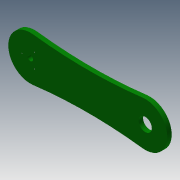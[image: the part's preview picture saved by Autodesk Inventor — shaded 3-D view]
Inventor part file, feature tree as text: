
AUTODESK INVENTOR PART (.ipt)
format: ipt  version: 2013 (Build 170138000, 138)  size: 303,104 bytes
history: native  units: mm
features: sketch x21, extrude x20
ambient origin geometry x8: Origin, YZ Plane, XZ Plane, XY Plane, X Axis, Y Axis, Z Axis, Center Point
bodies: Solid1 (feature_tree)
feature tree (41):
  extrude  "Extrusion1"  Depth=50.0mm
  extrude  "Extrusion2"  Depth=6.0mm
  extrude  "Extrusion3"  Depth=5.0mm TaperAngle=0.0deg
  extrude  "Extrusion4"  Depth=20.0mm
  extrude  "Extrusion5"  Depth=20.0mm
  extrude  "Extrusion6"  Depth=3.0mm
  sketch  "Sketch7"  dims[d22=3.0mm d23=5.0mm d24=0.0mm]
  extrude  "Extrusion7"  Depth=5.0mm TaperAngle=0.0deg
  extrude  "Extrusion8"  Depth=1.0mm
  extrude  "Extrusion9"  Depth=1.0mm
  extrude  "Extrusion10"  Depth=15.0mm
  extrude  "Extrusion11"  Depth=5.0mm TaperAngle=0.0deg
  sketch  "Sketch12"  dims[d44=1.0mm d45=1.0mm]
  sketch  "Sketch13"  dims[d46=1.0mm d47=5.0mm d48=0.0mm]
  extrude  "Extrusion12"  Depth=1.0mm
  extrude  "Extrusion13"  Depth=5.0mm TaperAngle=0.0deg
  extrude  "Extrusion14"  Depth=5.0mm TaperAngle=0.0deg
  extrude  "Extrusion15"  Depth=5.0mm TaperAngle=0.0deg
  extrude  "Extrusion16"  Depth=43.308mm
  extrude  "Extrusion18"  Depth=20.0mm
  extrude  "Extrusion19"  Depth=33.15mm
  extrude  "Extrusion20"  Depth=55.0mm
  extrude  "Extrusion21"  Depth=20.0mm
  sketch  "Sketch1"  dims[d0=150.0mm d1=50.0mm]
  sketch  "Sketch2"  dims[d2=5.0mm d3=0.0mm d4=6.0mm]
  sketch  "Sketch3"  dims[d5=6.0mm d6=5.0mm d7=0.0mm]
  sketch  "Sketch4"  dims[d11=55.0mm d12=20.0mm]
  sketch  "Sketch5"  dims[d13=40.2mm d14=20.0mm]
  sketch  "Sketch6"  dims[d20=3.0mm d21=3.0mm]
  sketch  "Sketch8"  dims[d32=5.0mm d33=0.0mm d34=1.0mm]
  sketch  "Sketch9"  dims[d35=1.0mm d36=1.0mm]
  sketch  "Sketch10"  dims[d37=5.0mm d38=0.0mm d39=15.0mm]
  sketch  "Sketch11"  dims[d40=15.0mm d41=5.0mm d42=0.0mm]
  sketch  "Sketch14"  dims[d49=5.0mm d50=0.0mm d51=5.0mm d52=0.0mm]
  sketch  "Sketch15"  dims[d53=130.0mm d54=5.0mm d55=0.0mm]
  sketch  "Sketch16"  dims[d56=15.0mm d57=43.308mm]
  sketch  "Sketch17"  dims[d58=40.2mm d59=20.0mm]
  sketch  "Sketch19"  dims[d60=5.0mm d61=0.0mm d62=33.15mm]
  sketch  "Sketch20"  dims[d63=18.1mm d64=55.0mm]
  sketch  "Sketch21"  dims[d65=40.2mm d66=20.0mm]
  sketch  "Sketch22"  dims[d67=5.0mm d68=0.0mm d69=33.15mm d70=18.1mm d71=55.0mm d72=40.2mm d73=20.0mm d74=5.0mm d75=0.0mm d76=5.0mm d77=0.0mm d84=5.0mm d85=0.0mm d86=5.0mm d87=0.0mm d98=6.0mm d99=5.0mm d100=0.0mm d101=19.075mm d102=2.0mm d103=60.0deg d104=60.0deg d105=2.0mm d106=2.0mm d107=5.0mm d108=0.0mm d109=1.0mm d110=1.0mm d111=1.0mm d112=5.0mm d113=0.0mm d114=5.0mm d115=0.0mm]
